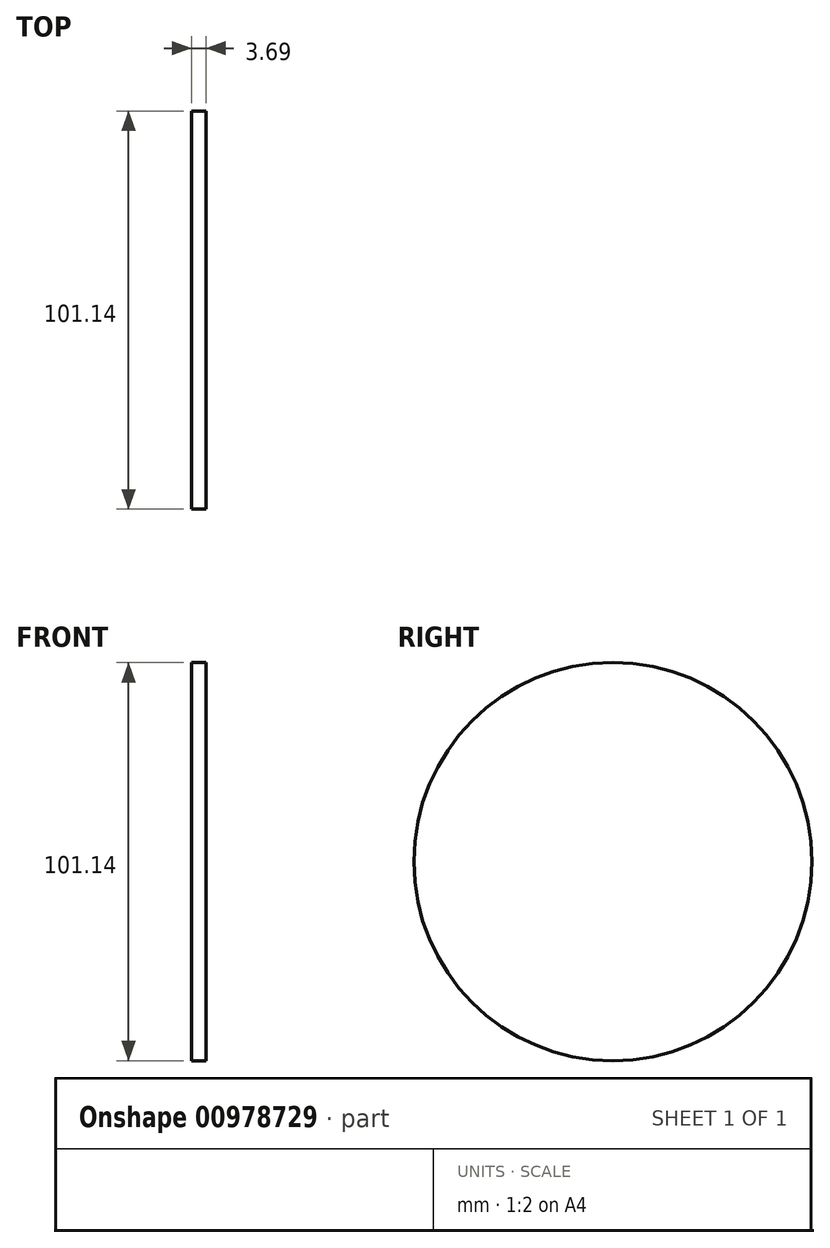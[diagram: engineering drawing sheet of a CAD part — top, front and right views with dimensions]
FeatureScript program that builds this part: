
annotation { "Feature Type Name" : "Feature", "Feature Type Description" : "" }
export const myFeature = defineFeature(function(context is Context, id is Id, definition is map)
    precondition{}
    {
        {
            var Q0;
            Q0=qCreatedBy(makeId("Right.planeOp"),FACE);
            var sketch = newSketch(context, id + "F0", { "sketchPlane" : qUnion([Q0])});
            skCircle(sketch, "E0", {"center": v(0, 0) * mm, "radius": 50.57 * mm});
            skSolve(sketch);
        }
        {
            var Q0;
            Q0=makeQuery(id+"F0.imprint","IMPRINT",FACE,{"disambiguationData":[TD([[makeQuery(id+"F0.imprint","IMPRINT",EDGE,{"derivedFrom":sQuery(id+"F0.wireOp",EDGE,"E0")}),1.0]])]});
            extrude(context, id + "F1", {"entities" : qUnion([Q0]), "depth" : 3.7 * mm, "offsetDistance" : 25.4 * mm});
        }
    });
